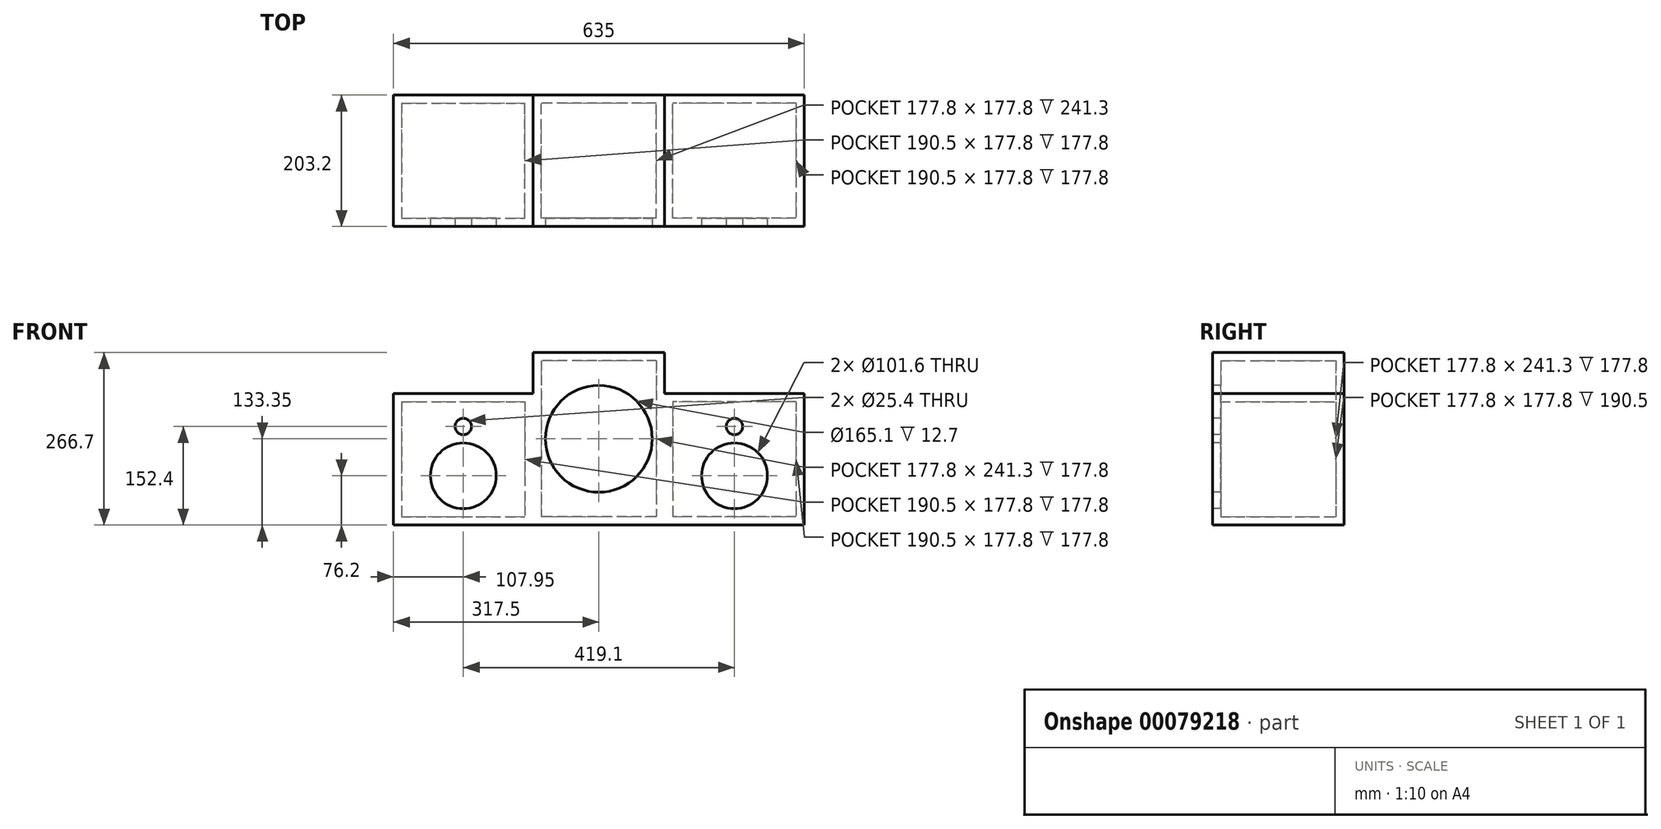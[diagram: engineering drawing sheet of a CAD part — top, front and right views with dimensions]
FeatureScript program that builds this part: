
annotation { "Feature Type Name" : "Feature", "Feature Type Description" : "" }
export const myFeature = defineFeature(function(context is Context, id is Id, definition is map)
    precondition{}
    {
        {
            var Q0;
            Q0=qCreatedBy(makeId("Top.planeOp"),FACE);
            var sketch = newSketch(context, id + "F0", { "sketchPlane" : qUnion([Q0])});
            skLineSegment(sketch, "E0.bottom", {"start": v(101.6, -101.6) * mm, "end": v(-101.6, -101.6) * mm});
            skLineSegment(sketch, "E0.top", {"start": v(101.6, 101.6) * mm, "end": v(-101.6, 101.6) * mm});
            skLineSegment(sketch, "E0.left", {"start": v(101.6, -101.6) * mm, "end": v(101.6, 101.6) * mm});
            skLineSegment(sketch, "E0.right", {"start": v(-101.6, -101.6) * mm, "end": v(-101.6, 101.6) * mm});
            skPoint(sketch, "E0.middle", {"position": v(0, 0) * mm});
            skSolve(sketch);
        }
        {
            var Q0;
            Q0=makeQuery(id+"F0.imprint","IMPRINT",FACE,{"disambiguationData":[TD([[makeQuery(id+"F0.imprint","IMPRINT",EDGE,{"derivedFrom":sQuery(id+"F0.wireOp",EDGE,"E0.bottom")}),-1.0]])]});
            extrude(context, id + "F1", {"entities" : qUnion([Q0]), "depth" : 12.7 * mm});
        }
        {
            var Q0;
            Q0=makeQuery(id+"F1.opExtrude","CAP_FACE",FACE,{"disambiguationData":[OSD([sQuery(id+"F0.wireOp",EDGE,"E0.bottom"),sQuery(id+"F0.wireOp",EDGE,"E0.top"),sQuery(id+"F0.wireOp",EDGE,"E0.left"),sQuery(id+"F0.wireOp",EDGE,"E0.right")])],"isStart":false});
            var sketch = newSketch(context, id + "F2", { "sketchPlane" : qUnion([Q0])});
            skLineSegment(sketch, "E1.0", {"start": v(88.9, 88.9) * mm, "end": v(-88.9, 88.9) * mm});
            skLineSegment(sketch, "E1.1", {"start": v(88.9, -88.9) * mm, "end": v(88.9, 88.9) * mm});
            skLineSegment(sketch, "E1.2", {"start": v(88.9, -88.9) * mm, "end": v(-88.9, -88.9) * mm});
            skLineSegment(sketch, "E1.3", {"start": v(-88.9, -88.9) * mm, "end": v(-88.9, 88.9) * mm});
            skSolve(sketch);
        }
        {
            var Q0;
            Q0=makeQuery(id+"F2.imprint","IMPRINT",FACE,{"disambiguationData":[TD([[makeQuery(id+"F2.imprint","IMPRINT",EDGE,{"derivedFrom":sQuery(id+"F2.wireOp",EDGE,"E1.0")}),-1.0]])]});
            extrude(context, id + "F3", {"entities" : qUnion([Q0]), "operationType" : NewBodyOperationType.ADD, "depth" : 254 * mm});
        }
        {
            var Q0;
            Q0=makeQuery(id+"F3.opExtrude","CAP_FACE",FACE,{"disambiguationData":[OSD([sQuery(id+"F0.wireOp",EDGE,"E0.bottom"),sQuery(id+"F0.wireOp",EDGE,"E0.top"),sQuery(id+"F0.wireOp",EDGE,"E0.left"),sQuery(id+"F0.wireOp",EDGE,"E0.right"),sQuery(id+"F2.wireOp",EDGE,"E1.0"),sQuery(id+"F2.wireOp",EDGE,"E1.1"),sQuery(id+"F2.wireOp",EDGE,"E1.2"),sQuery(id+"F2.wireOp",EDGE,"E1.3")])],"isStart":false});
            var sketch = newSketch(context, id + "F4", { "sketchPlane" : qUnion([Q0])});
            skLineSegment(sketch, "E2.bottom", {"start": v(-101.6, -101.6) * mm, "end": v(101.6, -101.6) * mm});
            skLineSegment(sketch, "E2.top", {"start": v(-101.6, 101.6) * mm, "end": v(101.6, 101.6) * mm});
            skLineSegment(sketch, "E2.left", {"start": v(-101.6, -101.6) * mm, "end": v(-101.6, 101.6) * mm});
            skLineSegment(sketch, "E2.right", {"start": v(101.6, -101.6) * mm, "end": v(101.6, 101.6) * mm});
            skSolve(sketch);
        }
        {
            var Q0;
            Q0=makeQuery(id+"F4.imprint","IMPRINT",FACE,{"disambiguationData":[TD([[makeQuery(id+"F4.imprint","IMPRINT",EDGE,{"derivedFrom":sQuery(id+"F4.wireOp",EDGE,"E2.bottom")}),-1.0]])]});
            var Q1;
            Q1=makeQuery(id+"F4.imprint","IMPRINT",FACE,{"disambiguationData":[TD([[makeQuery(id+"F4.imprint","IMPRINT",EDGE,{"derivedFrom":makeQuery(id+"F3.opExtrude","CAP_EDGE",EDGE,{"disambiguationData":[OSD([sQuery(id+"F2.wireOp",EDGE,"E1.0")])],"isStart":false})}),1.0]])]});
            extrude(context, id + "F5", {"entities" : qUnion([Q0, Q1]), "operationType" : NewBodyOperationType.ADD, "oppositeDirection" : true, "depth" : 12.7 * mm});
        }
        {
            var Q0;
            {var subQ0=sQuery(id+"F0.wireOp",EDGE,"E0.right");Q0=makeQuery(id+"F3.boolean.opBoolean","MERGE",FACE,{"derivedFrom":[makeQuery(id+"F1.opExtrude","SWEPT_FACE",FACE,{"disambiguationData":[OSD([subQ0])]}),makeQuery(id+"F3.opExtrude","SWEPT_FACE",FACE,{"disambiguationData":[OSD([subQ0])]})]});}
            var sketch = newSketch(context, id + "F6", { "sketchPlane" : qUnion([Q0])});
            skLineSegment(sketch, "E3.bottom", {"start": v(-101.6, 0) * mm, "end": v(101.6, 0) * mm});
            skLineSegment(sketch, "E3.top", {"start": v(-101.6, 203.2) * mm, "end": v(101.6, 203.2) * mm});
            skLineSegment(sketch, "E3.left", {"start": v(-101.6, 0) * mm, "end": v(-101.6, 203.2) * mm});
            skLineSegment(sketch, "E3.right", {"start": v(101.6, 0) * mm, "end": v(101.6, 203.2) * mm});
            skSolve(sketch);
        }
        {
            var Q0;
            Q0=makeQuery(id+"F6.imprint","IMPRINT",FACE,{"disambiguationData":[TD([[makeQuery(id+"F6.imprint","IMPRINT",EDGE,{"derivedFrom":sQuery(id+"F6.wireOp",EDGE,"E3.bottom")}),-1.0]])]});
            extrude(context, id + "F7", {"entities" : qUnion([Q0]), "operationType" : NewBodyOperationType.ADD, "depth" : 12.7 * mm});
        }
        {
            var Q0;
            Q0=makeQuery(id+"F7.opExtrude","CAP_FACE",FACE,{"disambiguationData":[OSD([sQuery(id+"F6.wireOp",EDGE,"E3.bottom"),sQuery(id+"F6.wireOp",EDGE,"E3.top"),sQuery(id+"F6.wireOp",EDGE,"E3.left"),sQuery(id+"F6.wireOp",EDGE,"E3.right")])],"isStart":false});
            var sketch = newSketch(context, id + "F8", { "sketchPlane" : qUnion([Q0])});
            skLineSegment(sketch, "E4.bottom", {"start": v(88.9, 190.5) * mm, "end": v(-88.9, 190.5) * mm});
            skLineSegment(sketch, "E4.top", {"start": v(88.9, 12.7) * mm, "end": v(-88.9, 12.7) * mm});
            skLineSegment(sketch, "E4.left", {"start": v(88.9, 190.5) * mm, "end": v(88.9, 12.7) * mm});
            skLineSegment(sketch, "E4.right", {"start": v(-88.9, 190.5) * mm, "end": v(-88.9, 12.7) * mm});
            skPoint(sketch, "E4.middle", {"position": v(0, 101.6) * mm});
            skPoint(sketch, "E4.middle.positionSnap0", {"position": v(-101.6, 101.6) * mm});
            skPoint(sketch, "E4.centerSnap0", {"position": v(-101.6, 101.6) * mm});
            skSolve(sketch);
        }
        {
            var Q0;
            Q0=makeQuery(id+"F8.imprint","IMPRINT",FACE,{"disambiguationData":[TD([[makeQuery(id+"F8.imprint","IMPRINT",EDGE,{"derivedFrom":sQuery(id+"F8.wireOp",EDGE,"E4.bottom")}),-1.0]])]});
            extrude(context, id + "F9", {"entities" : qUnion([Q0]), "operationType" : NewBodyOperationType.ADD, "depth" : 203.2 * mm});
        }
        {
            var Q0;
            Q0=makeQuery(id+"F9.opExtrude","SWEPT_FACE",FACE,{"disambiguationData":[OSD([sQuery(id+"F8.wireOp",EDGE,"E4.top")])]});
            var sketch = newSketch(context, id + "F10", { "sketchPlane" : qUnion([Q0])});
            skLineSegment(sketch, "E5.bottom", {"start": v(-317.5, 88.9) * mm, "end": v(-304.8, 88.9) * mm});
            skLineSegment(sketch, "E5.top", {"start": v(-317.5, -88.9) * mm, "end": v(-304.8, -88.9) * mm});
            skLineSegment(sketch, "E5.left", {"start": v(-317.5, 88.9) * mm, "end": v(-317.5, -88.9) * mm});
            skLineSegment(sketch, "E5.right", {"start": v(-304.8, 88.9) * mm, "end": v(-304.8, -88.9) * mm});
            skSolve(sketch);
        }
        {
            var Q0;
            Q0=makeQuery(id+"F10.imprint","IMPRINT",FACE,{"disambiguationData":[TD([[makeQuery(id+"F10.imprint","IMPRINT",EDGE,{"derivedFrom":sQuery(id+"F10.wireOp",EDGE,"E5.bottom")}),-1.0]])]});
            extrude(context, id + "F11", {"entities" : qUnion([Q0]), "operationType" : NewBodyOperationType.ADD, "depth" : 177.8 * mm});
        }
        {
            var Q0;
            {var subQ0=sQuery(id+"F6.wireOp",EDGE,"E3.right");var subQ1=sQuery(id+"F0.wireOp",EDGE,"E0.bottom");Q0=makeQuery(id+"F9.boolean.opBoolean","MERGE",FACE,{"derivedFrom":[makeQuery(id+"F7.boolean.opBoolean","MERGE",FACE,{"derivedFrom":[makeQuery(id+"F3.boolean.opBoolean","MERGE",FACE,{"derivedFrom":[makeQuery(id+"F1.opExtrude","SWEPT_FACE",FACE,{"disambiguationData":[OSD([subQ1])]}),makeQuery(id+"F3.opExtrude","SWEPT_FACE",FACE,{"disambiguationData":[OSD([subQ1])]})]}),makeQuery(id+"F7.opExtrude","SWEPT_FACE",FACE,{"disambiguationData":[OSD([subQ0])]})]}),makeQuery(id+"F9.opExtrude","SWEPT_FACE",FACE,{"disambiguationData":[OSD([subQ0])]})]});}
            var sketch = newSketch(context, id + "F12", { "sketchPlane" : qUnion([Q0])});
            skCircle(sketch, "E6", {"center": v(-209.55, 76.2) * mm, "radius": 50.8 * mm});
            skPoint(sketch, "E6.centerSnap0", {"position": v(-209.55, 203.2) * mm});
            skCircle(sketch, "E7", {"center": v(-209.55, 152.4) * mm, "radius": 12.7 * mm});
            skCircle(sketch, "E8", {"center": v(0, 133.35) * mm, "radius": 82.55 * mm});
            skPoint(sketch, "E8.centerSnap0", {"position": v(101.6, 133.35) * mm});
            skPoint(sketch, "E8.centerSnap1", {"position": v(0, 266.7) * mm});
            skLineSegment(sketch, "E9", {"start": v(0, 266.7) * mm, "end": v(0, 229.89) * mm});
            skSolve(sketch);
        }
        {
            var Q0;
            Q0=makeQuery(id+"F12.imprint","IMPRINT",FACE,{"disambiguationData":[TD([[makeQuery(id+"F12.imprint","IMPRINT",EDGE,{"derivedFrom":sQuery(id+"F12.wireOp",EDGE,"E6")}),1.0]])]});
            var Q1;
            Q1=makeQuery(id+"F12.imprint","IMPRINT",FACE,{"disambiguationData":[TD([[makeQuery(id+"F12.imprint","IMPRINT",EDGE,{"derivedFrom":sQuery(id+"F12.wireOp",EDGE,"E7")}),1.0]])]});
            var Q2;
            Q2=makeQuery(id+"F12.imprint","IMPRINT",FACE,{"disambiguationData":[TD([[makeQuery(id+"F12.imprint","IMPRINT",EDGE,{"derivedFrom":sQuery(id+"F12.wireOp",EDGE,"E8")}),1.0]])]});
            extrude(context, id + "F13", {"entities" : qUnion([Q0, Q1, Q2]), "operationType" : NewBodyOperationType.REMOVE, "oppositeDirection" : true, "depth" : 25.4 * mm});
        }
        {
            var Q0;
            {var subQ0=sQuery(id+"F6.wireOp",EDGE,"E3.right");var subQ1=sQuery(id+"F0.wireOp",EDGE,"E0.bottom");Q0=makeQuery(id+"F9.boolean.opBoolean","MERGE",FACE,{"derivedFrom":[makeQuery(id+"F7.boolean.opBoolean","MERGE",FACE,{"derivedFrom":[makeQuery(id+"F3.boolean.opBoolean","MERGE",FACE,{"derivedFrom":[makeQuery(id+"F1.opExtrude","SWEPT_FACE",FACE,{"disambiguationData":[OSD([subQ1])]}),makeQuery(id+"F3.opExtrude","SWEPT_FACE",FACE,{"disambiguationData":[OSD([subQ1])]})]}),makeQuery(id+"F7.opExtrude","SWEPT_FACE",FACE,{"disambiguationData":[OSD([subQ0])]})]}),makeQuery(id+"F9.opExtrude","SWEPT_FACE",FACE,{"disambiguationData":[OSD([subQ0])]})]});}
            var sketch = newSketch(context, id + "F14", { "sketchPlane" : qUnion([Q0])});
            skLineSegment(sketch, "E10.bottom", {"start": v(101.6, 266.7) * mm, "end": v(0, 266.7) * mm});
            skLineSegment(sketch, "E10.top", {"start": v(101.6, 0) * mm, "end": v(0, 0) * mm});
            skLineSegment(sketch, "E10.left", {"start": v(101.6, 266.7) * mm, "end": v(101.6, 0) * mm});
            skLineSegment(sketch, "E10.right", {"start": v(0, 266.7) * mm, "end": v(0, 0) * mm});
            skSolve(sketch);
        }
        {
            var Q0;
            {var subQ1=sQuery(id+"F14.wireOp",EDGE,"E10.bottom");Q0=makeQuery(id+"F14.imprint","IMPRINT",FACE,{"disambiguationData":[TD([[makeQuery(id+"F14.imprint","IMPRINT",EDGE,{"derivedFrom":subQ1}),1.0]])]});}
            var Q1;
            {var subQ0=sQuery(id+"F14.wireOp",EDGE,"E10.right");var subQ1=makeQuery(id+"F13.boolean.opBoolean","COPY",EDGE,{"derivedFrom":makeQuery(id+"F13.opExtrude","CAP_EDGE",EDGE,{"disambiguationData":[OSD([sQuery(id+"F12.wireOp",EDGE,"E8")])],"isStart":true})});var subQ2=makeQuery(id+"F14.imprint","INTERSECT",VERTEX,{"disambiguationData":[OD(0.0)],"derivedFrom":[subQ1,subQ0]});Q1=makeQuery(id+"F14.imprint","IMPRINT",FACE,{"disambiguationData":[TD([[makeQuery(id+"F14.imprint","IMPRINT",EDGE,{"disambiguationData":[TD([[subQ2,-1.0]])],"derivedFrom":subQ0}),1.0]])]});}
            extrude(context, id + "F15", {"entities" : qUnion([Q0, Q1]), "operationType" : NewBodyOperationType.REMOVE, "oppositeDirection" : true, "depth" : 203.2 * mm});
        }
        {
            var Q0;
            Q0=makeQuery(id+"F1.opExtrude","SWEPT_BODY",BODY,{"disambiguationData":[OSD([sQuery(id+"F0.wireOp",EDGE,"E0.bottom"),sQuery(id+"F0.wireOp",EDGE,"E0.top"),sQuery(id+"F0.wireOp",EDGE,"E0.left"),sQuery(id+"F0.wireOp",EDGE,"E0.right")])]});
            var Q1;
            Q1=makeQuery(id+"F15.boolean.opBoolean","COPY",FACE,{"derivedFrom":makeQuery(id+"F15.opExtrude","SWEPT_FACE",FACE,{"disambiguationData":[OSD([sQuery(id+"F14.wireOp",EDGE,"E10.right")])]})});
            mirror(context, id + "F16", {"operationType" : NewBodyOperationType.ADD, "entities" : qUnion([Q0]), "mirrorPlane" : qUnion([Q1])});
        }
    });
